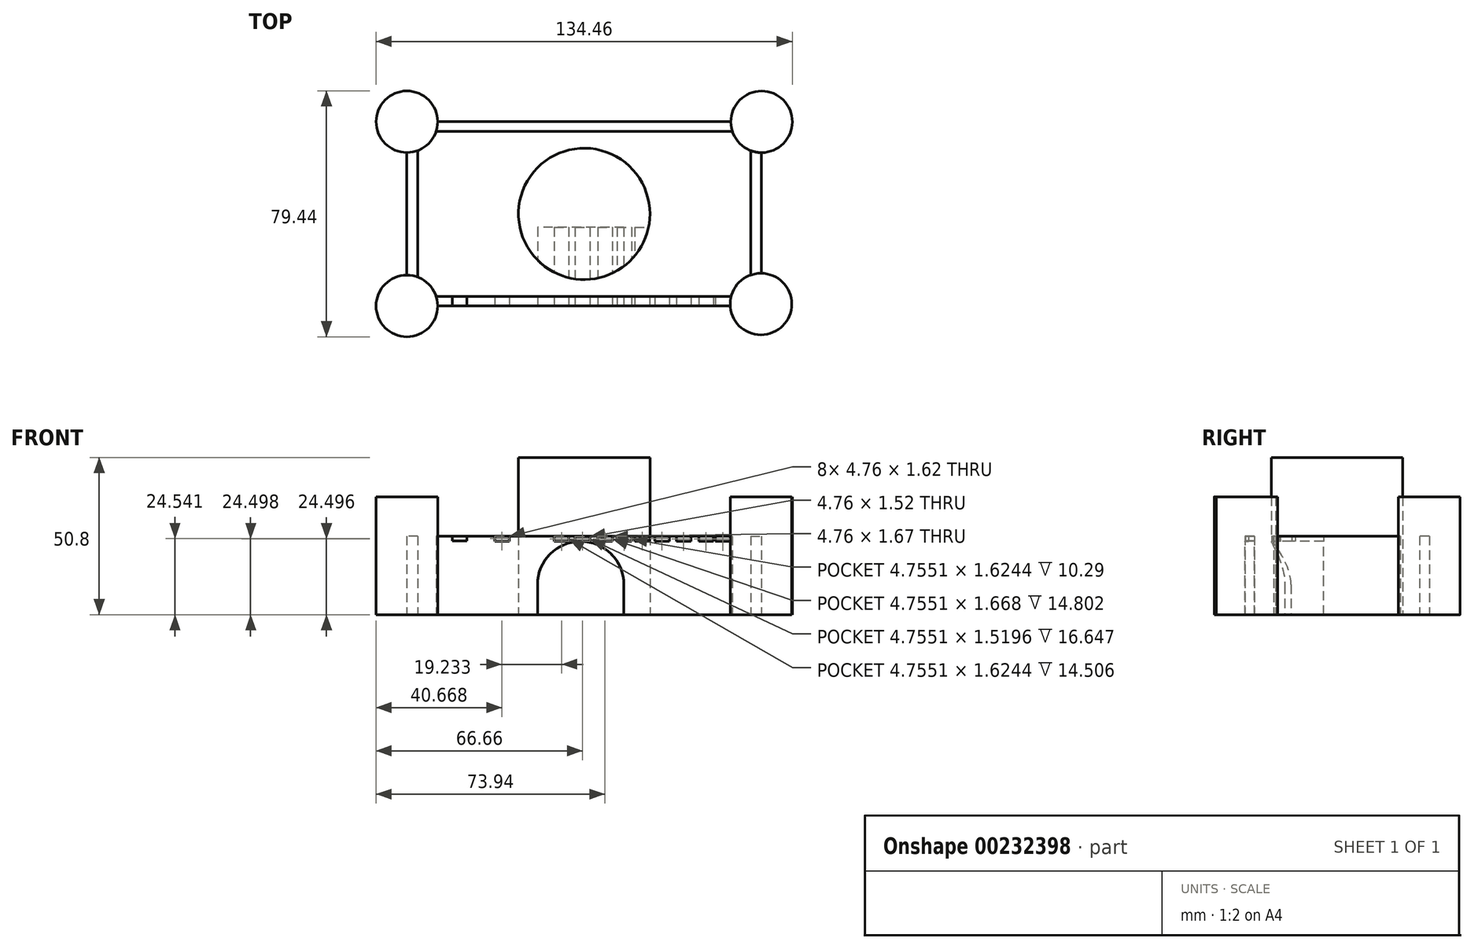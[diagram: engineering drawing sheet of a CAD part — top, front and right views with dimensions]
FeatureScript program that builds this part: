
annotation { "Feature Type Name" : "Feature", "Feature Type Description" : "" }
export const myFeature = defineFeature(function(context is Context, id is Id, definition is map)
    precondition{}
    {
        {
            var Q0;
            Q0=qCreatedBy(makeId("Top.planeOp"),FACE);
            var sketch = newSketch(context, id + "F0", { "sketchPlane" : qUnion([Q0])});
            skLineSegment(sketch, "E0.bottom", {"start": v(47.35, 29.77) * mm, "end": v(-47.32, 29.77) * mm});
            skLineSegment(sketch, "E0.top", {"start": v(47.16, -29.77) * mm, "end": v(-47.33, -29.77) * mm});
            skLineSegment(sketch, "E0.left", {"start": v(57.27, 19.8) * mm, "end": v(57.27, -19.2) * mm});
            skLineSegment(sketch, "E0.right", {"start": v(-57.27, 19.83) * mm, "end": v(-57.27, -19.82) * mm});
            skPoint(sketch, "E0.middle", {"position": v(0, 0) * mm});
            skCircle(sketch, "E1", {"center": v(0, 0) * mm, "radius": 21.22 * mm});
            skCircle(sketch, "E2", {"center": v(-57.27, 29.77) * mm, "radius": 9.95 * mm});
            skCircle(sketch, "E3", {"center": v(57.3, 29.74) * mm, "radius": 9.95 * mm});
            skCircle(sketch, "E4", {"center": v(57.08, -29.15) * mm, "radius": 9.95 * mm});
            skCircle(sketch, "E5", {"center": v(-57.28, -29.77) * mm, "radius": 9.95 * mm});
            skLineSegment(sketch, "E6.bottom", {"start": v(47.45, -26.67) * mm, "end": v(-47.83, -26.67) * mm});
            skLineSegment(sketch, "E6.top", {"start": v(47.83, 26.67) * mm, "end": v(-47.82, 26.67) * mm});
            skLineSegment(sketch, "E6.left", {"start": v(53.75, -19.78) * mm, "end": v(53.75, 20.45) * mm});
            skLineSegment(sketch, "E6.right", {"start": v(-53.75, -20.47) * mm, "end": v(-53.75, 20.47) * mm});
            skPoint(sketch, "E7.orphan", {"position": v(57.27, 29.77) * mm});
            skPoint(sketch, "E8.orphan", {"position": v(53.75, 26.67) * mm});
            skPoint(sketch, "E9.orphan", {"position": v(-53.75, 26.67) * mm});
            skPoint(sketch, "E10.orphan", {"position": v(-53.75, -26.67) * mm});
            skPoint(sketch, "E11.orphan", {"position": v(-57.27, -29.77) * mm});
            skPoint(sketch, "E12.orphan", {"position": v(53.75, -26.67) * mm});
            skPoint(sketch, "E13.orphan", {"position": v(57.27, -29.77) * mm});
            skSolve(sketch);
        }
        {
            var Q0;
            {var subQ0=sQuery(id+"F0.wireOp",EDGE,"E0.left");Q0=makeQuery(id+"F0.imprint","IMPRINT",FACE,{"disambiguationData":[TD([[makeQuery(id+"F0.imprint","IMPRINT",EDGE,{"derivedFrom":subQ0}),-1.0]])]});}
            var Q1;
            {var subQ0=sQuery(id+"F0.wireOp",EDGE,"E0.top");Q1=makeQuery(id+"F0.imprint","IMPRINT",FACE,{"disambiguationData":[TD([[makeQuery(id+"F0.imprint","IMPRINT",EDGE,{"derivedFrom":subQ0}),-1.0]])]});}
            var Q2;
            {var subQ0=sQuery(id+"F0.wireOp",EDGE,"E0.right");Q2=makeQuery(id+"F0.imprint","IMPRINT",FACE,{"disambiguationData":[TD([[makeQuery(id+"F0.imprint","IMPRINT",EDGE,{"derivedFrom":subQ0}),1.0]])]});}
            var Q3;
            {var subQ0=sQuery(id+"F0.wireOp",EDGE,"E0.bottom");Q3=makeQuery(id+"F0.imprint","IMPRINT",FACE,{"disambiguationData":[TD([[makeQuery(id+"F0.imprint","IMPRINT",EDGE,{"derivedFrom":subQ0}),1.0]])]});}
            extrude(context, id + "F1", {"entities" : qUnion([Q0, Q1, Q2, Q3]), "depth" : 25.4 * mm});
        }
        {
            var Q0;
            {var subQ0=sQuery(id+"F0.wireOp",EDGE,"E3");var subQ1=makeQuery(id+"F0.imprint","INTERSECT",VERTEX,{"derivedFrom":[sQuery(id+"F0.wireOp",EDGE,"E0.bottom"),subQ0]});Q0=makeQuery(id+"F0.imprint","IMPRINT",FACE,{"disambiguationData":[TD([[makeQuery(id+"F0.imprint","IMPRINT",EDGE,{"disambiguationData":[TD([[subQ1,-1.0]])],"derivedFrom":subQ0}),1.0]])]});}
            var Q1;
            {var subQ0=sQuery(id+"F0.wireOp",EDGE,"E4");var subQ1=makeQuery(id+"F0.imprint","INTERSECT",VERTEX,{"derivedFrom":[sQuery(id+"F0.wireOp",EDGE,"E0.left"),subQ0]});Q1=makeQuery(id+"F0.imprint","IMPRINT",FACE,{"disambiguationData":[TD([[makeQuery(id+"F0.imprint","IMPRINT",EDGE,{"disambiguationData":[TD([[subQ1,-1.0]])],"derivedFrom":subQ0}),1.0]])]});}
            var Q2;
            {var subQ0=sQuery(id+"F0.wireOp",EDGE,"E5");var subQ1=makeQuery(id+"F0.imprint","INTERSECT",VERTEX,{"derivedFrom":[subQ0,sQuery(id+"F0.wireOp",EDGE,"E6.bottom")]});Q2=makeQuery(id+"F0.imprint","IMPRINT",FACE,{"disambiguationData":[TD([[makeQuery(id+"F0.imprint","IMPRINT",EDGE,{"disambiguationData":[TD([[subQ1,-1.0]])],"derivedFrom":subQ0}),1.0]])]});}
            var Q3;
            {var subQ0=sQuery(id+"F0.wireOp",EDGE,"E2");var subQ1=makeQuery(id+"F0.imprint","INTERSECT",VERTEX,{"derivedFrom":[sQuery(id+"F0.wireOp",EDGE,"E0.bottom"),subQ0]});Q3=makeQuery(id+"F0.imprint","IMPRINT",FACE,{"disambiguationData":[TD([[makeQuery(id+"F0.imprint","IMPRINT",EDGE,{"disambiguationData":[TD([[subQ1,-1.0]])],"derivedFrom":subQ0}),1.0]])]});}
            extrude(context, id + "F2", {"entities" : qUnion([Q0, Q1, Q2, Q3]), "depth" : 38.1 * mm});
        }
        {
            var Q0;
            Q0=makeQuery(id+"F0.imprint","IMPRINT",FACE,{"disambiguationData":[TD([[makeQuery(id+"F0.imprint","IMPRINT",EDGE,{"derivedFrom":sQuery(id+"F0.wireOp",EDGE,"E1")}),1.0]])]});
            extrude(context, id + "F3", {"entities" : qUnion([Q0]), "depth" : 50.8 * mm});
        }
        {
            var Q0;
            Q0=makeQuery(id+"F1.opExtrude","SWEPT_FACE",FACE,{"disambiguationData":[OSD([sQuery(id+"F0.wireOp",EDGE,"E0.top")])]});
            var sketch = newSketch(context, id + "F4", { "sketchPlane" : qUnion([Q0])});
            skLineSegment(sketch, "E14.bottom", {"start": v(0, 0) * mm, "end": v(-15.1, 0) * mm});
            skLineSegment(sketch, "E14.top", {"start": v(0, 9.72) * mm, "end": v(-1.14, 9.72) * mm});
            skLineSegment(sketch, "E14.right", {"start": v(-15.1, 0) * mm, "end": v(-15.1, 9.72) * mm});
            skLineSegment(sketch, "E15.bottom", {"start": v(0, 0) * mm, "end": v(12.82, 0) * mm});
            skLineSegment(sketch, "E15.right", {"start": v(12.82, 0) * mm, "end": v(12.82, 9.72) * mm});
            skArc(sketch, "E16", {"start": v(12.82, 9.72) * mm, "mid": v(-1.14, 23.67) * mm, "end": v(-15.1, 9.72) * mm});
            skLineSegment(sketch, "E17.bottom", {"start": v(-42.59, 25.4) * mm, "end": v(-37.83, 25.4) * mm});
            skLineSegment(sketch, "E17.top", {"start": v(-42.59, 23.78) * mm, "end": v(-37.83, 23.78) * mm});
            skLineSegment(sketch, "E17.left", {"start": v(-42.59, 25.4) * mm, "end": v(-42.59, 23.78) * mm});
            skLineSegment(sketch, "E17.right", {"start": v(-37.83, 25.4) * mm, "end": v(-37.83, 23.78) * mm});
            skLineSegment(sketch, "E18.bottom", {"start": v(-40.21, 23.78) * mm, "end": v(-37.83, 23.78) * mm});
            skLineSegment(sketch, "E18.right", {"start": v(-37.83, 23.78) * mm, "end": v(-37.83, 24.59) * mm});
            skLineSegment(sketch, "E19.bottom", {"start": v(-35.55, 25.4) * mm, "end": v(-30.8, 25.4) * mm});
            skLineSegment(sketch, "E19.top", {"start": v(-35.55, 23.78) * mm, "end": v(-30.8, 23.78) * mm});
            skLineSegment(sketch, "E19.left", {"start": v(-35.55, 25.4) * mm, "end": v(-35.55, 23.78) * mm});
            skLineSegment(sketch, "E19.right", {"start": v(-30.8, 25.4) * mm, "end": v(-30.8, 23.78) * mm});
            skLineSegment(sketch, "E20.bottom", {"start": v(-33.17, 23.78) * mm, "end": v(-32.53, 23.78) * mm});
            skLineSegment(sketch, "E21.bottom", {"start": v(-28.93, 25.35) * mm, "end": v(-24.17, 25.35) * mm});
            skLineSegment(sketch, "E21.top", {"start": v(-28.93, 23.73) * mm, "end": v(-24.17, 23.73) * mm});
            skLineSegment(sketch, "E21.left", {"start": v(-28.93, 25.35) * mm, "end": v(-28.93, 23.73) * mm});
            skLineSegment(sketch, "E21.right", {"start": v(-24.17, 25.35) * mm, "end": v(-24.17, 23.73) * mm});
            skLineSegment(sketch, "E22.bottom", {"start": v(-26.55, 23.73) * mm, "end": v(-24.85, 23.73) * mm});
            skLineSegment(sketch, "E23.bottom", {"start": v(-22.37, 25.42) * mm, "end": v(-17.62, 25.42) * mm});
            skLineSegment(sketch, "E23.top", {"start": v(-22.37, 23.8) * mm, "end": v(-17.62, 23.8) * mm});
            skLineSegment(sketch, "E23.left", {"start": v(-22.37, 25.42) * mm, "end": v(-22.37, 23.8) * mm});
            skLineSegment(sketch, "E23.right", {"start": v(-17.62, 25.42) * mm, "end": v(-17.62, 23.8) * mm});
            skLineSegment(sketch, "E24.bottom", {"start": v(-20, 23.8) * mm, "end": v(-17.93, 23.8) * mm});
            skLineSegment(sketch, "E25.bottom", {"start": v(-16.06, 25.42) * mm, "end": v(-11.3, 25.42) * mm});
            skLineSegment(sketch, "E25.top", {"start": v(-16.06, 23.8) * mm, "end": v(-11.3, 23.8) * mm});
            skLineSegment(sketch, "E25.left", {"start": v(-16.06, 25.42) * mm, "end": v(-16.06, 23.8) * mm});
            skLineSegment(sketch, "E25.right", {"start": v(-11.3, 25.42) * mm, "end": v(-11.3, 23.8) * mm});
            skLineSegment(sketch, "E26.bottom", {"start": v(-13.68, 23.8) * mm, "end": v(-11.78, 23.8) * mm});
            skLineSegment(sketch, "E27.bottom", {"start": v(-9.7, 25.31) * mm, "end": v(-4.94, 25.31) * mm});
            skLineSegment(sketch, "E27.top", {"start": v(-9.7, 23.69) * mm, "end": v(-4.94, 23.69) * mm});
            skLineSegment(sketch, "E27.left", {"start": v(-9.7, 25.31) * mm, "end": v(-9.7, 23.69) * mm});
            skLineSegment(sketch, "E27.right", {"start": v(-4.94, 25.31) * mm, "end": v(-4.94, 23.69) * mm});
            skLineSegment(sketch, "E28.bottom", {"start": v(-2.94, 25.26) * mm, "end": v(1.82, 25.26) * mm});
            skLineSegment(sketch, "E28.top", {"start": v(-2.94, 23.74) * mm, "end": v(1.82, 23.74) * mm});
            skLineSegment(sketch, "E28.left", {"start": v(-2.94, 25.26) * mm, "end": v(-2.94, 23.74) * mm});
            skLineSegment(sketch, "E28.right", {"start": v(1.82, 25.26) * mm, "end": v(1.82, 23.74) * mm});
            skLineSegment(sketch, "E29.bottom", {"start": v(4.34, 25.33) * mm, "end": v(9.1, 25.33) * mm});
            skLineSegment(sketch, "E29.top", {"start": v(4.34, 23.66) * mm, "end": v(9.1, 23.66) * mm});
            skLineSegment(sketch, "E29.left", {"start": v(4.34, 25.33) * mm, "end": v(4.34, 23.66) * mm});
            skLineSegment(sketch, "E29.right", {"start": v(9.1, 25.33) * mm, "end": v(9.1, 23.66) * mm});
            skLineSegment(sketch, "E30.bottom", {"start": v(10.59, 25.32) * mm, "end": v(15.34, 25.32) * mm});
            skLineSegment(sketch, "E30.top", {"start": v(10.59, 23.7) * mm, "end": v(15.34, 23.7) * mm});
            skLineSegment(sketch, "E30.left", {"start": v(10.59, 25.32) * mm, "end": v(10.59, 23.7) * mm});
            skLineSegment(sketch, "E30.right", {"start": v(15.34, 25.32) * mm, "end": v(15.34, 23.7) * mm});
            skLineSegment(sketch, "E31.bottom", {"start": v(16.37, 25.36) * mm, "end": v(21.12, 25.36) * mm});
            skLineSegment(sketch, "E31.top", {"start": v(16.37, 23.74) * mm, "end": v(21.12, 23.74) * mm});
            skLineSegment(sketch, "E31.left", {"start": v(16.37, 25.36) * mm, "end": v(16.37, 23.74) * mm});
            skLineSegment(sketch, "E31.right", {"start": v(21.12, 25.36) * mm, "end": v(21.12, 23.74) * mm});
            skLineSegment(sketch, "E32.bottom", {"start": v(22.76, 25.37) * mm, "end": v(27.51, 25.37) * mm});
            skLineSegment(sketch, "E32.top", {"start": v(22.76, 23.75) * mm, "end": v(27.51, 23.75) * mm});
            skLineSegment(sketch, "E32.left", {"start": v(22.76, 25.37) * mm, "end": v(22.76, 23.75) * mm});
            skLineSegment(sketch, "E32.right", {"start": v(27.51, 25.37) * mm, "end": v(27.51, 23.75) * mm});
            skLineSegment(sketch, "E33.bottom", {"start": v(29.75, 25.3) * mm, "end": v(34.51, 25.3) * mm});
            skLineSegment(sketch, "E33.top", {"start": v(29.75, 23.67) * mm, "end": v(34.51, 23.67) * mm});
            skLineSegment(sketch, "E33.left", {"start": v(29.75, 25.3) * mm, "end": v(29.75, 23.67) * mm});
            skLineSegment(sketch, "E33.right", {"start": v(34.51, 25.3) * mm, "end": v(34.51, 23.67) * mm});
            skLineSegment(sketch, "E34.bottom", {"start": v(36.97, 25.3) * mm, "end": v(41.72, 25.3) * mm});
            skLineSegment(sketch, "E34.top", {"start": v(36.97, 23.67) * mm, "end": v(41.72, 23.67) * mm});
            skLineSegment(sketch, "E34.left", {"start": v(36.97, 25.3) * mm, "end": v(36.97, 23.67) * mm});
            skLineSegment(sketch, "E34.right", {"start": v(41.72, 25.3) * mm, "end": v(41.72, 23.67) * mm});
            skLineSegment(sketch, "E35.bottom", {"start": v(42.4, 25.32) * mm, "end": v(47.15, 25.32) * mm});
            skLineSegment(sketch, "E35.top", {"start": v(42.4, 23.7) * mm, "end": v(47.15, 23.7) * mm});
            skLineSegment(sketch, "E35.left", {"start": v(42.4, 25.32) * mm, "end": v(42.4, 23.7) * mm});
            skLineSegment(sketch, "E35.right", {"start": v(47.15, 25.32) * mm, "end": v(47.15, 23.7) * mm});
            skSolve(sketch);
        }
        {
            var Q0;
            Q0=makeQuery(id+"F4.imprint","IMPRINT",FACE,{"disambiguationData":[TD([[makeQuery(id+"F4.imprint","IMPRINT",EDGE,{"derivedFrom":sQuery(id+"F4.wireOp",EDGE,"E14.bottom")}),-1.0]])]});
            extrude(context, id + "F5", {"entities" : qUnion([Q0]), "operationType" : NewBodyOperationType.REMOVE, "oppositeDirection" : true, "depth" : 25.4 * mm});
        }
        {
            var Q0;
            Q0=makeQuery(id+"F4.imprint","IMPRINT",FACE,{"disambiguationData":[TD([[makeQuery(id+"F4.imprint","IMPRINT",EDGE,{"derivedFrom":sQuery(id+"F4.wireOp",EDGE,"E17.bottom")}),1.0]])]});
            var Q1;
            {var subQ8=sQuery(id+"F4.wireOp",EDGE,"E20.bottom");Q1=makeQuery(id+"F4.imprint","IMPRINT",FACE,{"disambiguationData":[TD([[makeQuery(id+"F4.imprint","IMPRINT",EDGE,{"derivedFrom":subQ8}),1.0]])]});}
            var Q2;
            Q2=makeQuery(id+"F4.imprint","IMPRINT",FACE,{"disambiguationData":[TD([[makeQuery(id+"F4.imprint","IMPRINT",EDGE,{"derivedFrom":sQuery(id+"F4.wireOp",EDGE,"E21.bottom")}),-1.0]])]});
            var Q3;
            {var subQ8=sQuery(id+"F4.wireOp",EDGE,"E24.bottom");Q3=makeQuery(id+"F4.imprint","IMPRINT",FACE,{"disambiguationData":[TD([[makeQuery(id+"F4.imprint","IMPRINT",EDGE,{"derivedFrom":subQ8}),1.0]])]});}
            var Q4;
            {var subQ8=sQuery(id+"F4.wireOp",EDGE,"E26.bottom");Q4=makeQuery(id+"F4.imprint","IMPRINT",FACE,{"disambiguationData":[TD([[makeQuery(id+"F4.imprint","IMPRINT",EDGE,{"derivedFrom":subQ8}),1.0]])]});}
            var Q5;
            Q5=makeQuery(id+"F4.imprint","IMPRINT",FACE,{"disambiguationData":[TD([[makeQuery(id+"F4.imprint","IMPRINT",EDGE,{"derivedFrom":sQuery(id+"F4.wireOp",EDGE,"E27.bottom")}),-1.0]])]});
            var Q6;
            Q6=makeQuery(id+"F4.imprint","IMPRINT",FACE,{"disambiguationData":[TD([[makeQuery(id+"F4.imprint","IMPRINT",EDGE,{"derivedFrom":sQuery(id+"F4.wireOp",EDGE,"E28.bottom")}),-1.0]])]});
            var Q7;
            Q7=makeQuery(id+"F4.imprint","IMPRINT",FACE,{"disambiguationData":[TD([[makeQuery(id+"F4.imprint","IMPRINT",EDGE,{"derivedFrom":sQuery(id+"F4.wireOp",EDGE,"E29.bottom")}),-1.0]])]});
            var Q8;
            Q8=makeQuery(id+"F4.imprint","IMPRINT",FACE,{"disambiguationData":[TD([[makeQuery(id+"F4.imprint","IMPRINT",EDGE,{"derivedFrom":sQuery(id+"F4.wireOp",EDGE,"E30.bottom")}),-1.0]])]});
            var Q9;
            Q9=makeQuery(id+"F4.imprint","IMPRINT",FACE,{"disambiguationData":[TD([[makeQuery(id+"F4.imprint","IMPRINT",EDGE,{"derivedFrom":sQuery(id+"F4.wireOp",EDGE,"E31.bottom")}),-1.0]])]});
            var Q10;
            Q10=makeQuery(id+"F4.imprint","IMPRINT",FACE,{"disambiguationData":[TD([[makeQuery(id+"F4.imprint","IMPRINT",EDGE,{"derivedFrom":sQuery(id+"F4.wireOp",EDGE,"E32.bottom")}),-1.0]])]});
            var Q11;
            Q11=makeQuery(id+"F4.imprint","IMPRINT",FACE,{"disambiguationData":[TD([[makeQuery(id+"F4.imprint","IMPRINT",EDGE,{"derivedFrom":sQuery(id+"F4.wireOp",EDGE,"E33.bottom")}),-1.0]])]});
            var Q12;
            Q12=makeQuery(id+"F4.imprint","IMPRINT",FACE,{"disambiguationData":[TD([[makeQuery(id+"F4.imprint","IMPRINT",EDGE,{"derivedFrom":sQuery(id+"F4.wireOp",EDGE,"E34.bottom")}),-1.0]])]});
            var Q13;
            Q13=makeQuery(id+"F4.imprint","IMPRINT",FACE,{"disambiguationData":[TD([[makeQuery(id+"F4.imprint","IMPRINT",EDGE,{"derivedFrom":sQuery(id+"F4.wireOp",EDGE,"E35.bottom")}),-1.0]])]});
            extrude(context, id + "F6", {"entities" : qUnion([Q0, Q1, Q2, Q3, Q4, Q5, Q6, Q7, Q8, Q9, Q10, Q11, Q12, Q13]), "operationType" : NewBodyOperationType.REMOVE, "oppositeDirection" : true, "depth" : 25.4 * mm});
        }
        {
            var Q0;
            Q0=makeQuery(id+"F4.imprint","IMPRINT",FACE,{"disambiguationData":[TD([[makeQuery(id+"F4.imprint","IMPRINT",EDGE,{"derivedFrom":sQuery(id+"F4.wireOp",EDGE,"E17.bottom")}),1.0]])]});
            var Q1;
            {var subQ8=sQuery(id+"F4.wireOp",EDGE,"E20.bottom");Q1=makeQuery(id+"F4.imprint","IMPRINT",FACE,{"disambiguationData":[TD([[makeQuery(id+"F4.imprint","IMPRINT",EDGE,{"derivedFrom":subQ8}),1.0]])]});}
            var Q2;
            Q2=makeQuery(id+"F4.imprint","IMPRINT",FACE,{"disambiguationData":[TD([[makeQuery(id+"F4.imprint","IMPRINT",EDGE,{"derivedFrom":sQuery(id+"F4.wireOp",EDGE,"E21.bottom")}),-1.0]])]});
            var Q3;
            {var subQ8=sQuery(id+"F4.wireOp",EDGE,"E24.bottom");Q3=makeQuery(id+"F4.imprint","IMPRINT",FACE,{"disambiguationData":[TD([[makeQuery(id+"F4.imprint","IMPRINT",EDGE,{"derivedFrom":subQ8}),1.0]])]});}
            var Q4;
            {var subQ8=sQuery(id+"F4.wireOp",EDGE,"E26.bottom");Q4=makeQuery(id+"F4.imprint","IMPRINT",FACE,{"disambiguationData":[TD([[makeQuery(id+"F4.imprint","IMPRINT",EDGE,{"derivedFrom":subQ8}),1.0]])]});}
            var Q5;
            Q5=makeQuery(id+"F4.imprint","IMPRINT",FACE,{"disambiguationData":[TD([[makeQuery(id+"F4.imprint","IMPRINT",EDGE,{"derivedFrom":sQuery(id+"F4.wireOp",EDGE,"E27.bottom")}),-1.0]])]});
            var Q6;
            Q6=makeQuery(id+"F4.imprint","IMPRINT",FACE,{"disambiguationData":[TD([[makeQuery(id+"F4.imprint","IMPRINT",EDGE,{"derivedFrom":sQuery(id+"F4.wireOp",EDGE,"E28.bottom")}),-1.0]])]});
            var Q7;
            Q7=makeQuery(id+"F4.imprint","IMPRINT",FACE,{"disambiguationData":[TD([[makeQuery(id+"F4.imprint","IMPRINT",EDGE,{"derivedFrom":sQuery(id+"F4.wireOp",EDGE,"E29.bottom")}),-1.0]])]});
            var Q8;
            Q8=makeQuery(id+"F4.imprint","IMPRINT",FACE,{"disambiguationData":[TD([[makeQuery(id+"F4.imprint","IMPRINT",EDGE,{"derivedFrom":sQuery(id+"F4.wireOp",EDGE,"E30.bottom")}),-1.0]])]});
            var Q9;
            Q9=makeQuery(id+"F4.imprint","IMPRINT",FACE,{"disambiguationData":[TD([[makeQuery(id+"F4.imprint","IMPRINT",EDGE,{"derivedFrom":sQuery(id+"F4.wireOp",EDGE,"E31.bottom")}),-1.0]])]});
            var Q10;
            Q10=makeQuery(id+"F4.imprint","IMPRINT",FACE,{"disambiguationData":[TD([[makeQuery(id+"F4.imprint","IMPRINT",EDGE,{"derivedFrom":sQuery(id+"F4.wireOp",EDGE,"E32.bottom")}),-1.0]])]});
            var Q11;
            Q11=makeQuery(id+"F4.imprint","IMPRINT",FACE,{"disambiguationData":[TD([[makeQuery(id+"F4.imprint","IMPRINT",EDGE,{"derivedFrom":sQuery(id+"F4.wireOp",EDGE,"E33.bottom")}),-1.0]])]});
            var Q12;
            Q12=makeQuery(id+"F4.imprint","IMPRINT",FACE,{"disambiguationData":[TD([[makeQuery(id+"F4.imprint","IMPRINT",EDGE,{"derivedFrom":sQuery(id+"F4.wireOp",EDGE,"E34.bottom")}),-1.0]])]});
            var Q13;
            Q13=makeQuery(id+"F4.imprint","IMPRINT",FACE,{"disambiguationData":[TD([[makeQuery(id+"F4.imprint","IMPRINT",EDGE,{"derivedFrom":sQuery(id+"F4.wireOp",EDGE,"E35.bottom")}),-1.0]])]});
            extrude(context, id + "F7", {"entities" : qUnion([Q0, Q1, Q2, Q3, Q4, Q5, Q6, Q7, Q8, Q9, Q10, Q11, Q12, Q13]), "operationType" : NewBodyOperationType.REMOVE, "oppositeDirection" : true, "depth" : 25.4 * mm});
        }
    });
